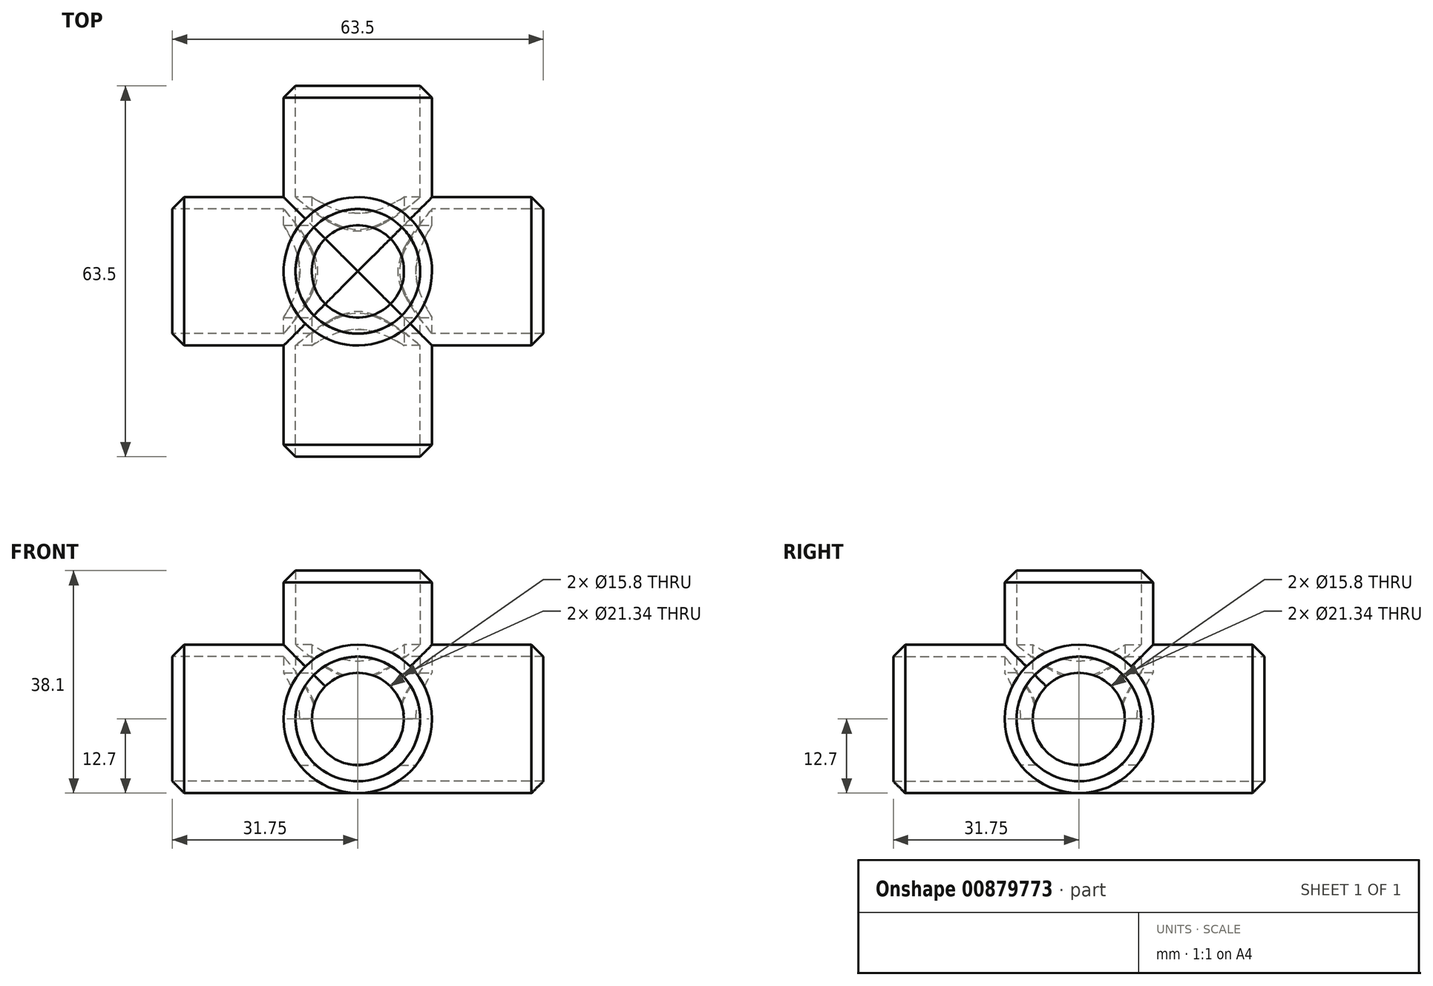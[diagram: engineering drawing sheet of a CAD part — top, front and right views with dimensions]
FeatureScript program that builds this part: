
annotation { "Feature Type Name" : "Feature", "Feature Type Description" : "" }
export const myFeature = defineFeature(function(context is Context, id is Id, definition is map)
    precondition{}
    {
        {
            var Q0;
            Q0=qCreatedBy(makeId("Front.planeOp"),FACE);
            var sketch = newSketch(context, id + "F0", { "sketchPlane" : qUnion([Q0])});
            skCircle(sketch, "E0", {"center": v(0, 0) * mm, "radius": 10.67 * mm});
            skCircle(sketch, "E1", {"center": v(0, 0) * mm, "radius": 12.7 * mm});
            skSolve(sketch);
        }
        {
            var Q0;
            Q0=makeQuery(id+"F0.imprint","IMPRINT",FACE,{"disambiguationData":[TD([[makeQuery(id+"F0.imprint","IMPRINT",EDGE,{"derivedFrom":sQuery(id+"F0.wireOp",EDGE,"E0")}),-1.0]])]});
            extrude(context, id + "F1", {"entities" : qUnion([Q0]), "depth" : 31.75 * mm, "offsetDistance" : 25.4 * mm, "hasSecondDirection" : true, "secondDirectionOppositeDirection" : true, "secondDirectionDepth" : 31.75 * mm});
        }
        {
            var Q0;
            Q0=qCreatedBy(makeId("Right.planeOp"),FACE);
            var sketch = newSketch(context, id + "F2", { "sketchPlane" : qUnion([Q0])});
            skCircle(sketch, "E2", {"center": v(0, 0) * mm, "radius": 10.67 * mm});
            skCircle(sketch, "E3", {"center": v(0, 0) * mm, "radius": 12.7 * mm});
            skSolve(sketch);
        }
        {
            var Q0;
            Q0 = qSketchRegion(id + "F2", true);
            extrude(context, id + "F3", {"entities" : qUnion([Q0]), "operationType" : NewBodyOperationType.ADD, "depth" : 31.75 * mm, "offsetDistance" : 25.4 * mm, "hasSecondDirection" : true, "secondDirectionOppositeDirection" : true, "secondDirectionDepth" : 31.75 * mm});
        }
        {
            var Q0;
            Q0=qCreatedBy(makeId("Top.planeOp"),FACE);
            var sketch = newSketch(context, id + "F4", { "sketchPlane" : qUnion([Q0])});
            skCircle(sketch, "E4", {"center": v(0, 0) * mm, "radius": 10.67 * mm});
            skCircle(sketch, "E5", {"center": v(0, 0) * mm, "radius": 12.7 * mm});
            skSolve(sketch);
        }
        {
            var Q0;
            Q0 = qSketchRegion(id + "F4", true);
            extrude(context, id + "F5", {"entities" : qUnion([Q0]), "operationType" : NewBodyOperationType.ADD, "depth" : 25.4 * mm, "offsetDistance" : 25.4 * mm});
        }
        {
            var Q0;
            Q0=makeQuery(id+"F3.opExtrude","CAP_EDGE",EDGE,{"disambiguationData":[OSD([sQuery(id+"F2.wireOp",EDGE,"E3")])],"isStart":true});
            var Q1;
            Q1=makeQuery(id+"F1.opExtrude","CAP_EDGE",EDGE,{"disambiguationData":[OSD([sQuery(id+"F0.wireOp",EDGE,"E1")])],"isStart":false});
            var Q2;
            Q2=makeQuery(id+"F3.opExtrude","CAP_EDGE",EDGE,{"disambiguationData":[OSD([sQuery(id+"F2.wireOp",EDGE,"E3")])],"isStart":false});
            var Q3;
            Q3=makeQuery(id+"F1.opExtrude","CAP_EDGE",EDGE,{"disambiguationData":[OSD([sQuery(id+"F0.wireOp",EDGE,"E1")])],"isStart":true});
            var Q4;
            Q4=makeQuery(id+"F5.opExtrude","CAP_EDGE",EDGE,{"disambiguationData":[OSD([sQuery(id+"F4.wireOp",EDGE,"E5")])],"isStart":false});
            chamfer(context, id + "F6", {"entities" : qUnion([Q0, Q1, Q2, Q3, Q4]), "width" : 2.03 * mm, "tangentPropagation" : true});
        }
        {
            var Q0;
            Q0=qCreatedBy(makeId("Front.planeOp"),FACE);
            var sketch = newSketch(context, id + "F7", { "sketchPlane" : qUnion([Q0])});
            skCircle(sketch, "E6", {"center": v(0, 0) * mm, "radius": 7.9 * mm});
            skSolve(sketch);
        }
        {
            var Q0;
            Q0 = qSketchRegion(id + "F7", true);
            extrude(context, id + "F8", {"entities" : qUnion([Q0]), "operationType" : NewBodyOperationType.REMOVE, "oppositeDirection" : true, "depth" : 25.4 * mm, "offsetDistance" : 25.4 * mm, "hasSecondDirection" : true, "secondDirectionOppositeDirection" : false, "secondDirectionDepth" : 25.4 * mm});
        }
        {
            var Q0;
            Q0=qCreatedBy(makeId("Right.planeOp"),FACE);
            var sketch = newSketch(context, id + "F9", { "sketchPlane" : qUnion([Q0])});
            skCircle(sketch, "E7", {"center": v(0, 0) * mm, "radius": 7.9 * mm});
            skSolve(sketch);
        }
        {
            var Q0;
            Q0 = qSketchRegion(id + "F9", true);
            extrude(context, id + "F10", {"entities" : qUnion([Q0]), "operationType" : NewBodyOperationType.REMOVE, "oppositeDirection" : true, "depth" : 25.4 * mm, "offsetDistance" : 25.4 * mm, "hasSecondDirection" : true, "secondDirectionOppositeDirection" : false, "secondDirectionDepth" : 25.4 * mm});
        }
        {
            var Q0;
            Q0=qCreatedBy(makeId("Top.planeOp"),FACE);
            var sketch = newSketch(context, id + "F11", { "sketchPlane" : qUnion([Q0])});
            skCircle(sketch, "E8", {"center": v(0, 0) * mm, "radius": 7.9 * mm});
            skSolve(sketch);
        }
        {
            var Q0;
            Q0 = qSketchRegion(id + "F11", true);
            extrude(context, id + "F12", {"entities" : qUnion([Q0]), "operationType" : NewBodyOperationType.REMOVE, "depth" : 25.4 * mm, "offsetDistance" : 25.4 * mm});
        }
    });
